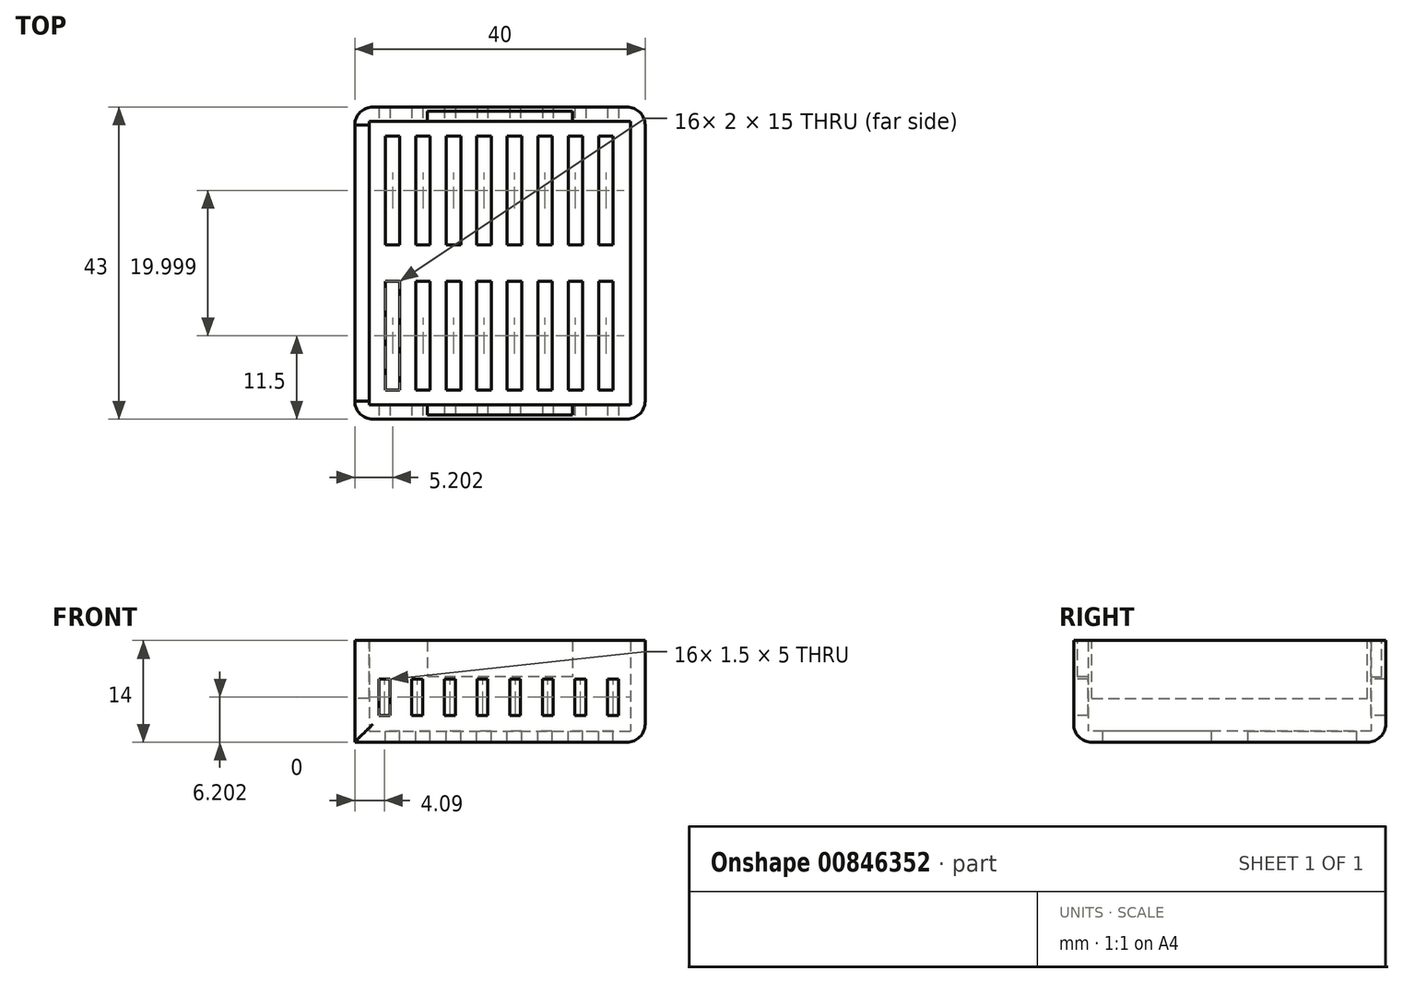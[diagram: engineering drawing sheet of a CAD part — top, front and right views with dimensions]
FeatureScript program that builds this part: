
annotation { "Feature Type Name" : "Feature", "Feature Type Description" : "" }
export const myFeature = defineFeature(function(context is Context, id is Id, definition is map)
    precondition{}
    {
        {
            var Q0;
            Q0=qCreatedBy(makeId("Top.planeOp"),FACE);
            var sketch = newSketch(context, id + "F0", { "sketchPlane" : qUnion([Q0])});
            skLineSegment(sketch, "E0.bottom", {"start": v(18, -19.5) * mm, "end": v(-18, -19.5) * mm});
            skLineSegment(sketch, "E0.top", {"start": v(18, 19.5) * mm, "end": v(-18, 19.5) * mm});
            skLineSegment(sketch, "E0.left", {"start": v(18, -19.5) * mm, "end": v(18, 19.5) * mm});
            skLineSegment(sketch, "E0.right", {"start": v(-18, -19.5) * mm, "end": v(-18, 19.5) * mm});
            skPoint(sketch, "E0.middle", {"position": v(0, 0) * mm});
            skLineSegment(sketch, "E1.bottom", {"start": v(20, -21.5) * mm, "end": v(-20, -21.5) * mm});
            skLineSegment(sketch, "E1.top", {"start": v(20, 21.5) * mm, "end": v(-20, 21.5) * mm});
            skLineSegment(sketch, "E1.left", {"start": v(20, -21.5) * mm, "end": v(20, 21.5) * mm});
            skLineSegment(sketch, "E1.right", {"start": v(-20, -21.5) * mm, "end": v(-20, 21.5) * mm});
            skSolve(sketch);
        }
        {
            var Q0;
            Q0=makeQuery(id+"F0.imprint","IMPRINT",FACE,{"disambiguationData":[TD([[makeQuery(id+"F0.imprint","IMPRINT",EDGE,{"derivedFrom":sQuery(id+"F0.wireOp",EDGE,"E0.bottom")}),-1.0]])]});
            var Q1;
            Q1=makeQuery(id+"F0.imprint","IMPRINT",FACE,{"disambiguationData":[TD([[makeQuery(id+"F0.imprint","IMPRINT",EDGE,{"derivedFrom":sQuery(id+"F0.wireOp",EDGE,"E0.bottom")}),1.0]])]});
            extrude(context, id + "F1", {"entities" : qUnion([Q0, Q1]), "depth" : 1.5 * mm, "offsetDistance" : 25 * mm});
        }
        {
            var Q0;
            Q0=makeQuery(id+"F0.imprint","IMPRINT",FACE,{"disambiguationData":[TD([[makeQuery(id+"F0.imprint","IMPRINT",EDGE,{"derivedFrom":sQuery(id+"F0.wireOp",EDGE,"E0.bottom")}),1.0]])]});
            extrude(context, id + "F2", {"entities" : qUnion([Q0]), "operationType" : NewBodyOperationType.ADD, "depth" : 14 * mm, "offsetDistance" : 25 * mm});
        }
        {
            var Q0;
            Q0=makeQuery(id+"F2.opExtrude","CAP_FACE",FACE,{"disambiguationData":[OSD([sQuery(id+"F0.wireOp",EDGE,"E0.bottom"),sQuery(id+"F0.wireOp",EDGE,"E0.top"),sQuery(id+"F0.wireOp",EDGE,"E0.left"),sQuery(id+"F0.wireOp",EDGE,"E0.right"),sQuery(id+"F0.wireOp",EDGE,"E1.bottom"),sQuery(id+"F0.wireOp",EDGE,"E1.top"),sQuery(id+"F0.wireOp",EDGE,"E1.left"),sQuery(id+"F0.wireOp",EDGE,"E1.right")])],"isStart":false});
            var sketch = newSketch(context, id + "F3", { "sketchPlane" : qUnion([Q0])});
            skLineSegment(sketch, "E2.bottom", {"start": v(-15.12, -19) * mm, "end": v(-20.12, -19) * mm});
            skLineSegment(sketch, "E2.top", {"start": v(-15.12, 19) * mm, "end": v(-20.12, 19) * mm});
            skLineSegment(sketch, "E2.left", {"start": v(-15.12, -19) * mm, "end": v(-15.12, 19) * mm});
            skLineSegment(sketch, "E2.right", {"start": v(-20.12, -19) * mm, "end": v(-20.12, 19) * mm});
            skPoint(sketch, "E2.middle", {"position": v(-17.62, 0) * mm});
            skPoint(sketch, "E2.middle.positionSnap0", {"position": v(-20, 0) * mm});
            skPoint(sketch, "E2.centerSnap0", {"position": v(-20, 0) * mm});
            skSolve(sketch);
        }
        {
            var Q0;
            {var subQ0=sQuery(id+"F3.wireOp",EDGE,"E2.bottom");var subQ1=makeQuery(id+"F2.opExtrude","CAP_EDGE",EDGE,{"disambiguationData":[OSD([sQuery(id+"F0.wireOp",EDGE,"E1.right")])],"isStart":false});var subQ2=makeQuery(id+"F3.imprint","INTERSECT",VERTEX,{"derivedFrom":[subQ1,subQ0]});Q0=makeQuery(id+"F3.imprint","IMPRINT",FACE,{"disambiguationData":[TD([[makeQuery(id+"F3.imprint","IMPRINT",EDGE,{"disambiguationData":[TD([[subQ2,1.0]])],"derivedFrom":subQ0}),-1.0]])]});}
            extrude(context, id + "F4", {"entities" : qUnion([Q0]), "operationType" : NewBodyOperationType.REMOVE, "oppositeDirection" : true, "depth" : 8 * mm, "offsetDistance" : 25 * mm});
        }
        {
            var Q0;
            {var subQ0=sQuery(id+"F0.wireOp",EDGE,"E1.right");var subQ1=sQuery(id+"F0.wireOp",EDGE,"E1.bottom");Q0=makeQuery(id+"F2.boolean.opBoolean","MERGE",EDGE,{"derivedFrom":[makeQuery(id+"F1.opExtrude","SWEPT_EDGE",EDGE,{"disambiguationData":[OSD([subQ1,subQ0])]}),makeQuery(id+"F2.opExtrude","SWEPT_EDGE",EDGE,{"disambiguationData":[OSD([subQ1,subQ0])]})]});}
            var Q1;
            {var subQ0=sQuery(id+"F0.wireOp",EDGE,"E1.left");var subQ1=sQuery(id+"F0.wireOp",EDGE,"E1.bottom");Q1=makeQuery(id+"F2.boolean.opBoolean","MERGE",EDGE,{"derivedFrom":[makeQuery(id+"F1.opExtrude","SWEPT_EDGE",EDGE,{"disambiguationData":[OSD([subQ1,subQ0])]}),makeQuery(id+"F2.opExtrude","SWEPT_EDGE",EDGE,{"disambiguationData":[OSD([subQ1,subQ0])]})]});}
            var Q2;
            {var subQ0=sQuery(id+"F0.wireOp",EDGE,"E1.left");var subQ1=sQuery(id+"F0.wireOp",EDGE,"E1.top");Q2=makeQuery(id+"F2.boolean.opBoolean","MERGE",EDGE,{"derivedFrom":[makeQuery(id+"F1.opExtrude","SWEPT_EDGE",EDGE,{"disambiguationData":[OSD([subQ1,subQ0])]}),makeQuery(id+"F2.opExtrude","SWEPT_EDGE",EDGE,{"disambiguationData":[OSD([subQ1,subQ0])]})]});}
            var Q3;
            {var subQ0=sQuery(id+"F0.wireOp",EDGE,"E1.right");var subQ1=sQuery(id+"F0.wireOp",EDGE,"E1.top");Q3=makeQuery(id+"F2.boolean.opBoolean","MERGE",EDGE,{"derivedFrom":[makeQuery(id+"F1.opExtrude","SWEPT_EDGE",EDGE,{"disambiguationData":[OSD([subQ1,subQ0])]}),makeQuery(id+"F2.opExtrude","SWEPT_EDGE",EDGE,{"disambiguationData":[OSD([subQ1,subQ0])]})]});}
            var Q4;
            Q4=makeQuery(id+"F1.opExtrude","CAP_EDGE",EDGE,{"disambiguationData":[OSD([sQuery(id+"F0.wireOp",EDGE,"E1.bottom")])],"isStart":true});
            var Q5;
            Q5=makeQuery(id+"F1.opExtrude","CAP_EDGE",EDGE,{"disambiguationData":[OSD([sQuery(id+"F0.wireOp",EDGE,"E1.left")])],"isStart":true});
            var Q6;
            Q6=makeQuery(id+"F1.opExtrude","CAP_EDGE",EDGE,{"disambiguationData":[OSD([sQuery(id+"F0.wireOp",EDGE,"E1.top")])],"isStart":true});
            fillet(context, id + "F5", {"entities" : qUnion([Q0, Q1, Q2, Q3, Q4, Q5, Q6]), "radius" : 2.5 * mm, "tangentPropagation" : true, "allowEdgeOverflow" : false});
        }
        {
            var Q0;
            Q0=makeQuery(id+"F2.opExtrude","CAP_FACE",FACE,{"disambiguationData":[OSD([sQuery(id+"F0.wireOp",EDGE,"E0.bottom"),sQuery(id+"F0.wireOp",EDGE,"E0.top"),sQuery(id+"F0.wireOp",EDGE,"E0.left"),sQuery(id+"F0.wireOp",EDGE,"E0.right"),sQuery(id+"F0.wireOp",EDGE,"E1.bottom"),sQuery(id+"F0.wireOp",EDGE,"E1.top"),sQuery(id+"F0.wireOp",EDGE,"E1.left"),sQuery(id+"F0.wireOp",EDGE,"E1.right")])],"isStart":false});
            var sketch = newSketch(context, id + "F6", { "sketchPlane" : qUnion([Q0])});
            skLineSegment(sketch, "E3.bottom", {"start": v(10, 19.45) * mm, "end": v(-10, 19.45) * mm});
            skLineSegment(sketch, "E3.top", {"start": v(10, 20.95) * mm, "end": v(-10, 20.95) * mm});
            skLineSegment(sketch, "E3.left", {"start": v(10, 19.45) * mm, "end": v(10, 20.95) * mm});
            skLineSegment(sketch, "E3.right", {"start": v(-10, 19.45) * mm, "end": v(-10, 20.95) * mm});
            skPoint(sketch, "E3.middle", {"position": v(0, 20.2) * mm});
            skLineSegment(sketch, "E4.MirrorCS", {"start": v(-10, -19.45) * mm, "end": v(-10, -20.95) * mm});
            skLineSegment(sketch, "E5.MirrorCS", {"start": v(10, -19.45) * mm, "end": v(10, -20.95) * mm});
            skLineSegment(sketch, "E6.MirrorCS", {"start": v(10, -20.95) * mm, "end": v(-10, -20.95) * mm});
            skLineSegment(sketch, "E7.MirrorCS", {"start": v(10, -19.45) * mm, "end": v(-10, -19.45) * mm});
            skPoint(sketch, "E8.MirrorP", {"position": v(0, -20.2) * mm});
            skSolve(sketch);
        }
        {
            var Q0;
            Q0=makeQuery(id+"F6.imprint","IMPRINT",FACE,{"disambiguationData":[TD([[makeQuery(id+"F6.imprint","IMPRINT",EDGE,{"derivedFrom":sQuery(id+"F6.wireOp",EDGE,"E3.bottom")}),-1.0]])]});
            var Q1;
            Q1=makeQuery(id+"F6.imprint","IMPRINT",FACE,{"disambiguationData":[TD([[makeQuery(id+"F6.imprint","IMPRINT",EDGE,{"derivedFrom":sQuery(id+"F6.wireOp",EDGE,"E4.MirrorCS")}),1.0]])]});
            var Q2;
            {var subQ0=sQuery(id+"F6.wireOp",EDGE,"E3.top");Q2=makeQuery(id+"F6.imprint","IMPRINT",FACE,{"disambiguationData":[TD([[makeQuery(id+"F6.imprint","IMPRINT",EDGE,{"derivedFrom":subQ0}),1.0]])]});}
            extrude(context, id + "F7", {"entities" : qUnion([Q0, Q1, Q2]), "operationType" : NewBodyOperationType.REMOVE, "oppositeDirection" : true, "depth" : 5 * mm, "offsetDistance" : 25 * mm});
        }
        {
            var Q0;
            Q0=makeQuery(id+"F1.opExtrude","CAP_FACE",FACE,{"disambiguationData":[OSD([sQuery(id+"F0.wireOp",EDGE,"E1.bottom"),sQuery(id+"F0.wireOp",EDGE,"E1.top"),sQuery(id+"F0.wireOp",EDGE,"E1.left"),sQuery(id+"F0.wireOp",EDGE,"E1.right")])],"isStart":false});
            var sketch = newSketch(context, id + "F8", { "sketchPlane" : qUnion([Q0])});
            skLineSegment(sketch, "E9.bottom", {"start": v(-13.8, 2.5) * mm, "end": v(-15.8, 2.5) * mm});
            skLineSegment(sketch, "E9.top", {"start": v(-13.8, 17.5) * mm, "end": v(-15.8, 17.5) * mm});
            skLineSegment(sketch, "E9.left", {"start": v(-13.8, 2.5) * mm, "end": v(-13.8, 17.5) * mm});
            skLineSegment(sketch, "E9.right", {"start": v(-15.8, 2.5) * mm, "end": v(-15.8, 17.5) * mm});
            skPoint(sketch, "E9.middle", {"position": v(-14.8, 10) * mm});
            skLineSegment(sketch, "E10.MirrorCS", {"start": v(-13.8, -2.5) * mm, "end": v(-15.8, -2.5) * mm});
            skLineSegment(sketch, "E11.MirrorCS", {"start": v(-13.8, -17.5) * mm, "end": v(-15.8, -17.5) * mm});
            skLineSegment(sketch, "E12.MirrorCS", {"start": v(-13.8, -2.5) * mm, "end": v(-13.8, -17.5) * mm});
            skLineSegment(sketch, "E13.MirrorCS", {"start": v(-15.8, -2.5) * mm, "end": v(-15.8, -17.5) * mm});
            skPoint(sketch, "E14.MirrorP", {"position": v(-14.8, -10) * mm});
            skLineSegment(sketch, "E15.1.0.0", {"start": v(-11.6, 2.5) * mm, "end": v(-11.6, 17.5) * mm});
            skLineSegment(sketch, "E15.1.0.1", {"start": v(-9.6, 2.5) * mm, "end": v(-9.6, 17.5) * mm});
            skPoint(sketch, "E15.1.0.2", {"position": v(-10.6, 10) * mm});
            skLineSegment(sketch, "E15.1.0.3", {"start": v(-9.6, 2.5) * mm, "end": v(-11.6, 2.5) * mm});
            skLineSegment(sketch, "E15.1.0.4", {"start": v(-9.6, 17.5) * mm, "end": v(-11.6, 17.5) * mm});
            skPoint(sketch, "E15.1.0.5", {"position": v(-10.6, -10) * mm});
            skLineSegment(sketch, "E15.1.0.6", {"start": v(-9.6, -2.5) * mm, "end": v(-9.6, -17.5) * mm});
            skLineSegment(sketch, "E15.1.0.7", {"start": v(-9.6, -2.5) * mm, "end": v(-11.6, -2.5) * mm});
            skLineSegment(sketch, "E15.1.0.8", {"start": v(-11.6, -2.5) * mm, "end": v(-11.6, -17.5) * mm});
            skLineSegment(sketch, "E15.1.0.9", {"start": v(-9.6, -17.5) * mm, "end": v(-11.6, -17.5) * mm});
            skLineSegment(sketch, "E15.2.0.0", {"start": v(-7.4, 2.5) * mm, "end": v(-7.4, 17.5) * mm});
            skLineSegment(sketch, "E15.2.0.1", {"start": v(-5.4, 2.5) * mm, "end": v(-5.4, 17.5) * mm});
            skPoint(sketch, "E15.2.0.2", {"position": v(-6.4, 10) * mm});
            skLineSegment(sketch, "E15.2.0.3", {"start": v(-5.4, 2.5) * mm, "end": v(-7.4, 2.5) * mm});
            skLineSegment(sketch, "E15.2.0.4", {"start": v(-5.4, 17.5) * mm, "end": v(-7.4, 17.5) * mm});
            skPoint(sketch, "E15.2.0.5", {"position": v(-6.4, -10) * mm});
            skLineSegment(sketch, "E15.2.0.6", {"start": v(-5.4, -2.5) * mm, "end": v(-5.4, -17.5) * mm});
            skLineSegment(sketch, "E15.2.0.7", {"start": v(-5.4, -2.5) * mm, "end": v(-7.4, -2.5) * mm});
            skLineSegment(sketch, "E15.2.0.8", {"start": v(-7.4, -2.5) * mm, "end": v(-7.4, -17.5) * mm});
            skLineSegment(sketch, "E15.2.0.9", {"start": v(-5.4, -17.5) * mm, "end": v(-7.4, -17.5) * mm});
            skLineSegment(sketch, "E15.3.0.0", {"start": v(-3.2, 2.5) * mm, "end": v(-3.2, 17.5) * mm});
            skLineSegment(sketch, "E15.3.0.1", {"start": v(-1.2, 2.5) * mm, "end": v(-1.2, 17.5) * mm});
            skPoint(sketch, "E15.3.0.2", {"position": v(-2.2, 10) * mm});
            skLineSegment(sketch, "E15.3.0.3", {"start": v(-1.2, 2.5) * mm, "end": v(-3.2, 2.5) * mm});
            skLineSegment(sketch, "E15.3.0.4", {"start": v(-1.2, 17.5) * mm, "end": v(-3.2, 17.5) * mm});
            skPoint(sketch, "E15.3.0.5", {"position": v(-2.2, -10) * mm});
            skLineSegment(sketch, "E15.3.0.6", {"start": v(-1.2, -2.5) * mm, "end": v(-1.2, -17.5) * mm});
            skLineSegment(sketch, "E15.3.0.7", {"start": v(-1.2, -2.5) * mm, "end": v(-3.2, -2.5) * mm});
            skLineSegment(sketch, "E15.3.0.8", {"start": v(-3.2, -2.5) * mm, "end": v(-3.2, -17.5) * mm});
            skLineSegment(sketch, "E15.3.0.9", {"start": v(-1.2, -17.5) * mm, "end": v(-3.2, -17.5) * mm});
            skLineSegment(sketch, "E15.4.0.0", {"start": v(1, 2.5) * mm, "end": v(1, 17.5) * mm});
            skLineSegment(sketch, "E15.4.0.1", {"start": v(3, 2.5) * mm, "end": v(3, 17.5) * mm});
            skPoint(sketch, "E15.4.0.2", {"position": v(2, 10) * mm});
            skLineSegment(sketch, "E15.4.0.3", {"start": v(3, 2.5) * mm, "end": v(1, 2.5) * mm});
            skLineSegment(sketch, "E15.4.0.4", {"start": v(3, 17.5) * mm, "end": v(1, 17.5) * mm});
            skPoint(sketch, "E15.4.0.5", {"position": v(2, -10) * mm});
            skLineSegment(sketch, "E15.4.0.6", {"start": v(3, -2.5) * mm, "end": v(3, -17.5) * mm});
            skLineSegment(sketch, "E15.4.0.7", {"start": v(3, -2.5) * mm, "end": v(1, -2.5) * mm});
            skLineSegment(sketch, "E15.4.0.8", {"start": v(1, -2.5) * mm, "end": v(1, -17.5) * mm});
            skLineSegment(sketch, "E15.4.0.9", {"start": v(3, -17.5) * mm, "end": v(1, -17.5) * mm});
            skLineSegment(sketch, "E15.5.0.0", {"start": v(5.2, 2.5) * mm, "end": v(5.2, 17.5) * mm});
            skLineSegment(sketch, "E15.5.0.1", {"start": v(7.2, 2.5) * mm, "end": v(7.2, 17.5) * mm});
            skPoint(sketch, "E15.5.0.2", {"position": v(6.2, 10) * mm});
            skLineSegment(sketch, "E15.5.0.3", {"start": v(7.2, 2.5) * mm, "end": v(5.2, 2.5) * mm});
            skLineSegment(sketch, "E15.5.0.4", {"start": v(7.2, 17.5) * mm, "end": v(5.2, 17.5) * mm});
            skPoint(sketch, "E15.5.0.5", {"position": v(6.2, -10) * mm});
            skLineSegment(sketch, "E15.5.0.6", {"start": v(7.2, -2.5) * mm, "end": v(7.2, -17.5) * mm});
            skLineSegment(sketch, "E15.5.0.7", {"start": v(7.2, -2.5) * mm, "end": v(5.2, -2.5) * mm});
            skLineSegment(sketch, "E15.5.0.8", {"start": v(5.2, -2.5) * mm, "end": v(5.2, -17.5) * mm});
            skLineSegment(sketch, "E15.5.0.9", {"start": v(7.2, -17.5) * mm, "end": v(5.2, -17.5) * mm});
            skLineSegment(sketch, "E15.6.0.0", {"start": v(9.4, 2.5) * mm, "end": v(9.4, 17.5) * mm});
            skLineSegment(sketch, "E15.6.0.1", {"start": v(11.4, 2.5) * mm, "end": v(11.4, 17.5) * mm});
            skPoint(sketch, "E15.6.0.2", {"position": v(10.4, 10) * mm});
            skLineSegment(sketch, "E15.6.0.3", {"start": v(11.4, 2.5) * mm, "end": v(9.4, 2.5) * mm});
            skLineSegment(sketch, "E15.6.0.4", {"start": v(11.4, 17.5) * mm, "end": v(9.4, 17.5) * mm});
            skPoint(sketch, "E15.6.0.5", {"position": v(10.4, -10) * mm});
            skLineSegment(sketch, "E15.6.0.6", {"start": v(11.4, -2.5) * mm, "end": v(11.4, -17.5) * mm});
            skLineSegment(sketch, "E15.6.0.7", {"start": v(11.4, -2.5) * mm, "end": v(9.4, -2.5) * mm});
            skLineSegment(sketch, "E15.6.0.8", {"start": v(9.4, -2.5) * mm, "end": v(9.4, -17.5) * mm});
            skLineSegment(sketch, "E15.6.0.9", {"start": v(11.4, -17.5) * mm, "end": v(9.4, -17.5) * mm});
            skLineSegment(sketch, "E15.7.0.0", {"start": v(13.6, 2.5) * mm, "end": v(13.6, 17.5) * mm});
            skLineSegment(sketch, "E15.7.0.1", {"start": v(15.6, 2.5) * mm, "end": v(15.6, 17.5) * mm});
            skPoint(sketch, "E15.7.0.2", {"position": v(14.6, 10) * mm});
            skLineSegment(sketch, "E15.7.0.3", {"start": v(15.6, 2.5) * mm, "end": v(13.6, 2.5) * mm});
            skLineSegment(sketch, "E15.7.0.4", {"start": v(15.6, 17.5) * mm, "end": v(13.6, 17.5) * mm});
            skPoint(sketch, "E15.7.0.5", {"position": v(14.6, -10) * mm});
            skLineSegment(sketch, "E15.7.0.6", {"start": v(15.6, -2.5) * mm, "end": v(15.6, -17.5) * mm});
            skLineSegment(sketch, "E15.7.0.7", {"start": v(15.6, -2.5) * mm, "end": v(13.6, -2.5) * mm});
            skLineSegment(sketch, "E15.7.0.8", {"start": v(13.6, -2.5) * mm, "end": v(13.6, -17.5) * mm});
            skLineSegment(sketch, "E15.7.0.9", {"start": v(15.6, -17.5) * mm, "end": v(13.6, -17.5) * mm});
            skLineSegment(sketch, "E15.direction1", {"start": v(-15.8, -17.5) * mm, "end": v(-11.6, -17.5) * mm, "construction": true});
            skSolve(sketch);
        }
        {
            var Q0;
            Q0 = qSketchRegion(id + "F8", true);
            extrude(context, id + "F9", {"entities" : qUnion([Q0]), "operationType" : NewBodyOperationType.REMOVE, "oppositeDirection" : true, "depth" : 25 * mm, "offsetDistance" : 25 * mm});
        }
        {
            var Q0;
            {var subQ0=sQuery(id+"F0.wireOp",EDGE,"E1.bottom");Q0=makeQuery(id+"F2.boolean.opBoolean","MERGE",FACE,{"derivedFrom":[makeQuery(id+"F1.opExtrude","SWEPT_FACE",FACE,{"disambiguationData":[OSD([subQ0])]}),makeQuery(id+"F2.opExtrude","SWEPT_FACE",FACE,{"disambiguationData":[OSD([subQ0])]})]});}
            var sketch = newSketch(context, id + "F10", { "sketchPlane" : qUnion([Q0])});
            skLineSegment(sketch, "E16.bottom", {"start": v(-15.16, 3.7) * mm, "end": v(-16.66, 3.7) * mm});
            skLineSegment(sketch, "E16.top", {"start": v(-15.16, 8.7) * mm, "end": v(-16.66, 8.7) * mm});
            skLineSegment(sketch, "E16.left", {"start": v(-15.16, 3.7) * mm, "end": v(-15.16, 8.7) * mm});
            skLineSegment(sketch, "E16.right", {"start": v(-16.66, 3.7) * mm, "end": v(-16.66, 8.7) * mm});
            skPoint(sketch, "E16.middle", {"position": v(-15.91, 6.2) * mm});
            skLineSegment(sketch, "E17.1.0.0", {"start": v(-10.66, 3.7) * mm, "end": v(-10.66, 8.7) * mm});
            skLineSegment(sketch, "E17.1.0.1", {"start": v(-10.66, 8.7) * mm, "end": v(-12.16, 8.7) * mm});
            skLineSegment(sketch, "E17.1.0.2", {"start": v(-10.66, 3.7) * mm, "end": v(-12.16, 3.7) * mm});
            skLineSegment(sketch, "E17.1.0.3", {"start": v(-12.16, 3.7) * mm, "end": v(-12.16, 8.7) * mm});
            skPoint(sketch, "E17.1.0.4", {"position": v(-11.41, 6.2) * mm});
            skLineSegment(sketch, "E17.2.0.0", {"start": v(-6.16, 3.7) * mm, "end": v(-6.16, 8.7) * mm});
            skLineSegment(sketch, "E17.2.0.1", {"start": v(-6.16, 8.7) * mm, "end": v(-7.66, 8.7) * mm});
            skLineSegment(sketch, "E17.2.0.2", {"start": v(-6.16, 3.7) * mm, "end": v(-7.66, 3.7) * mm});
            skLineSegment(sketch, "E17.2.0.3", {"start": v(-7.66, 3.7) * mm, "end": v(-7.66, 8.7) * mm});
            skPoint(sketch, "E17.2.0.4", {"position": v(-6.91, 6.2) * mm});
            skLineSegment(sketch, "E17.3.0.0", {"start": v(-1.66, 3.7) * mm, "end": v(-1.66, 8.7) * mm});
            skLineSegment(sketch, "E17.3.0.1", {"start": v(-1.66, 8.7) * mm, "end": v(-3.16, 8.7) * mm});
            skLineSegment(sketch, "E17.3.0.2", {"start": v(-1.66, 3.7) * mm, "end": v(-3.16, 3.7) * mm});
            skLineSegment(sketch, "E17.3.0.3", {"start": v(-3.16, 3.7) * mm, "end": v(-3.16, 8.7) * mm});
            skPoint(sketch, "E17.3.0.4", {"position": v(-2.41, 6.2) * mm});
            skLineSegment(sketch, "E17.4.0.0", {"start": v(2.84, 3.7) * mm, "end": v(2.84, 8.7) * mm});
            skLineSegment(sketch, "E17.4.0.1", {"start": v(2.84, 8.7) * mm, "end": v(1.34, 8.7) * mm});
            skLineSegment(sketch, "E17.4.0.2", {"start": v(2.84, 3.7) * mm, "end": v(1.34, 3.7) * mm});
            skLineSegment(sketch, "E17.4.0.3", {"start": v(1.34, 3.7) * mm, "end": v(1.34, 8.7) * mm});
            skPoint(sketch, "E17.4.0.4", {"position": v(2.09, 6.2) * mm});
            skLineSegment(sketch, "E17.5.0.0", {"start": v(7.34, 3.7) * mm, "end": v(7.34, 8.7) * mm});
            skLineSegment(sketch, "E17.5.0.1", {"start": v(7.34, 8.7) * mm, "end": v(5.84, 8.7) * mm});
            skLineSegment(sketch, "E17.5.0.2", {"start": v(7.34, 3.7) * mm, "end": v(5.84, 3.7) * mm});
            skLineSegment(sketch, "E17.5.0.3", {"start": v(5.84, 3.7) * mm, "end": v(5.84, 8.7) * mm});
            skPoint(sketch, "E17.5.0.4", {"position": v(6.59, 6.2) * mm});
            skLineSegment(sketch, "E17.6.0.0", {"start": v(11.84, 3.7) * mm, "end": v(11.84, 8.7) * mm});
            skLineSegment(sketch, "E17.6.0.1", {"start": v(11.84, 8.7) * mm, "end": v(10.34, 8.7) * mm});
            skLineSegment(sketch, "E17.6.0.2", {"start": v(11.84, 3.7) * mm, "end": v(10.34, 3.7) * mm});
            skLineSegment(sketch, "E17.6.0.3", {"start": v(10.34, 3.7) * mm, "end": v(10.34, 8.7) * mm});
            skPoint(sketch, "E17.6.0.4", {"position": v(11.09, 6.2) * mm});
            skLineSegment(sketch, "E17.7.0.0", {"start": v(16.34, 3.7) * mm, "end": v(16.34, 8.7) * mm});
            skLineSegment(sketch, "E17.7.0.1", {"start": v(16.34, 8.7) * mm, "end": v(14.84, 8.7) * mm});
            skLineSegment(sketch, "E17.7.0.2", {"start": v(16.34, 3.7) * mm, "end": v(14.84, 3.7) * mm});
            skLineSegment(sketch, "E17.7.0.3", {"start": v(14.84, 3.7) * mm, "end": v(14.84, 8.7) * mm});
            skPoint(sketch, "E17.7.0.4", {"position": v(15.59, 6.2) * mm});
            skLineSegment(sketch, "E17.direction1", {"start": v(-16.66, 3.7) * mm, "end": v(-12.16, 3.7) * mm, "construction": true});
            skSolve(sketch);
        }
        {
            var Q0;
            Q0 = qSketchRegion(id + "F10", true);
            extrude(context, id + "F11", {"entities" : qUnion([Q0]), "operationType" : NewBodyOperationType.REMOVE, "oppositeDirection" : true, "depth" : 50 * mm, "offsetDistance" : 25 * mm});
        }
    });
